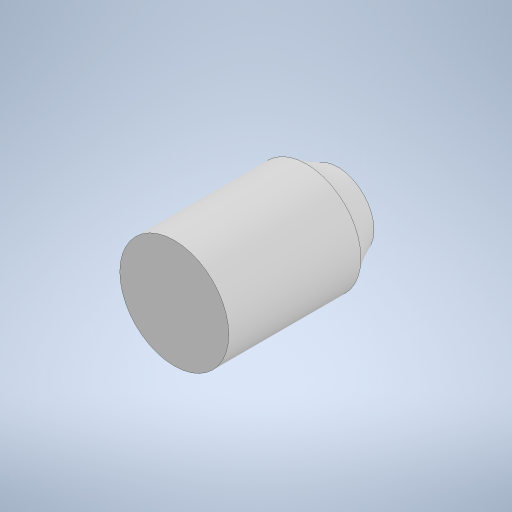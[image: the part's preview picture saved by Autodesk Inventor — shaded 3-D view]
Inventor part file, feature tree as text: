
AUTODESK INVENTOR PART (.ipt)
format: ipt  version: 2024 (Build 280153000, 153)  size: 263,680 bytes
history: native  units: in
note: dims shown in document units (in); Inventor stores cm internally (conversion verified against a paired STEP export)
features: extrude x6, sketch x6, projected_geometry x4, fillet x1
ambient origin geometry x8: Origin, YZ Plane, XZ Plane, XY Plane, X Axis, Y Axis, Z Axis, Center Point
bodies: Solid1 (feature_tree)
feature tree (17):
  extrude  "Extrusion1"  Depth=0.25in
  extrude  "Extrusion2"  Depth=0.75in
  extrude  "Extrusion4"  Depth=0.25in TaperAngle=0.0deg
  extrude  "Extrusion5"  Depth=0.375in TaperAngle=0.0deg
  extrude  "Extrusion6"  Depth=0.4375in
  fillet  "Fillet2"  Radius=0.375in
  extrude  "Extrusion7"  [1 undecoded]
  sketch  "Sketch1"  dims[d0=0.1969in d1=0.25in]
  sketch  "Sketch2"  dims[d2=0.25in d3=0.0in d4=0.75in]
  sketch  "Sketch4"  dims[d5=0.8571in d6=0.25in d7=0.0in]
  projected_geometry  "Projected Loop2"
  sketch  "Sketch5"  dims[d11=0.0625in d12=0.0in d13=0.375in d14=0.0in]
  projected_geometry  "Projected Loop3"
  sketch  "Sketch6"  dims[d15=0.255in d16=0.0in d17=0.4375in d18=0.375in]
  projected_geometry  "Projected Loop4"
  sketch  "Sketch7"  dims[d19=0.62in d20=0.0in]
  projected_geometry  "Projected Loop5"
note: 1 required parameter value undecoded (feature->parameter linkage not recoverable at this tier; creation-order binding heuristic only, values carry confidence <= 0.55)
